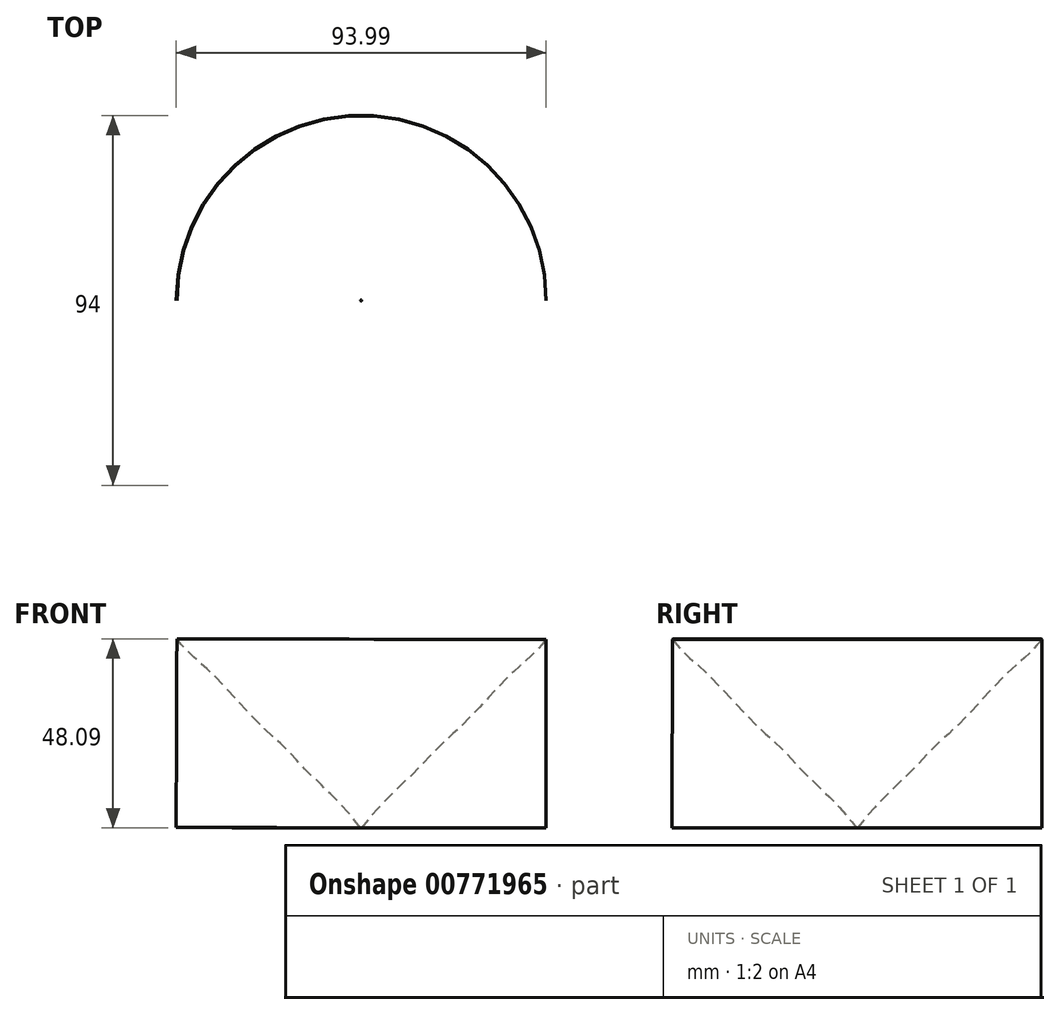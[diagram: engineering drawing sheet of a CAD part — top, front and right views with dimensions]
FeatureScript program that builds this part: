
annotation { "Feature Type Name" : "Feature", "Feature Type Description" : "" }
export const myFeature = defineFeature(function(context is Context, id is Id, definition is map)
    precondition{}
    {
        {
            var Q0;
            Q0=qCreatedBy(makeId("Front.planeOp"),FACE);
            var sketch = newSketch(context, id + "F0", { "sketchPlane" : qUnion([Q0])});
            skPoint(sketch, "E0", {"position": v(0, 1.93) * mm});
            skPoint(sketch, "E1", {"position": v(1.69, 2.62) * mm});
            skPoint(sketch, "E2", {"position": v(3.49, 4.29) * mm});
            skPoint(sketch, "E3", {"position": v(5.84, 6.5) * mm});
            skPoint(sketch, "E4", {"position": v(7.23, 8.44) * mm});
            skPoint(sketch, "E5", {"position": v(9.45, 10.38) * mm});
            skPoint(sketch, "E6", {"position": v(12.08, 12.73) * mm});
            skPoint(sketch, "E7", {"position": v(13.32, 14.26) * mm});
            skPoint(sketch, "E8", {"position": v(14.7, 15.5) * mm});
            skPoint(sketch, "E9", {"position": v(15.95, 16.61) * mm});
            skPoint(sketch, "E10", {"position": v(17.06, 17.72) * mm});
            skPoint(sketch, "E11", {"position": v(18.3, 19.38) * mm});
            skPoint(sketch, "E12", {"position": v(19.7, 20.77) * mm});
            skPoint(sketch, "E13", {"position": v(20.94, 21.74) * mm});
            skPoint(sketch, "E14", {"position": v(22.33, 23.12) * mm});
            skPoint(sketch, "E15", {"position": v(24.27, 24.92) * mm});
            skPoint(sketch, "E16", {"position": v(25.51, 26.59) * mm});
            skPoint(sketch, "E17", {"position": v(26.9, 27.7) * mm});
            skPoint(sketch, "E18", {"position": v(28.7, 29.77) * mm});
            skPoint(sketch, "E19", {"position": v(30.64, 31.43) * mm});
            skPoint(sketch, "E20", {"position": v(32.3, 33.23) * mm});
            skPoint(sketch, "E21", {"position": v(33.4, 34.48) * mm});
            skPoint(sketch, "E22", {"position": v(34.51, 35.87) * mm});
            skPoint(sketch, "E23", {"position": v(36.45, 38.08) * mm});
            skPoint(sketch, "E24", {"position": v(38.53, 39.74) * mm});
            skPoint(sketch, "E25", {"position": v(40.6, 41.4) * mm});
            skPoint(sketch, "E26", {"position": v(41.72, 42.51) * mm});
            skPoint(sketch, "E27", {"position": v(43.38, 43.9) * mm});
            skPoint(sketch, "E28", {"position": v(45.04, 45.7) * mm});
            skPoint(sketch, "E29", {"position": v(46.86, 46.8) * mm});
            skFitSpline(sketch, "E30", {"points": [v(0, 0) * mm, v(3.49, 4.29) * mm, v(9.45, 10.38) * mm, v(14.7, 15.5) * mm, v(19.7, 20.77) * mm, v(24.27, 24.92) * mm, v(30.64, 31.43) * mm, v(38.53, 39.74) * mm, v(41.72, 42.51) * mm, v(45.04, 45.7) * mm, v(46.86, 47.91) * mm], "startDerivative": vector(34.23, 44.37) * mm, "endDerivative": vector(24.25, 31.62) * mm});
            skLineSegment(sketch, "E31", {"start": v(46.86, 47.91) * mm, "end": v(46.86, 0) * mm});
            skLineSegment(sketch, "E32", {"start": v(46.86, 0) * mm, "end": v(0, 0) * mm, "construction": true});
            skLineSegment(sketch, "E33", {"start": v(46.86, 0) * mm, "end": v(0, 0) * mm});
            skLineSegment(sketch, "E34", {"start": v(0, 0) * mm, "end": v(0, 50.25) * mm});
            skLineSegment(sketch, "E35", {"start": v(0, 1.93) * mm, "end": v(0.17, 1.93) * mm});
            skLineSegment(sketch, "E36", {"start": v(0, 0) * mm, "end": v(0, 59.37) * mm});
            skLineSegment(sketch, "E37", {"start": v(-0.13, 0) * mm, "end": v(0, 68.57) * mm});
            skSolve(sketch);
        }
        {
            var Q0;
            Q0=makeQuery(id+"F0.imprint","IMPRINT",FACE,{"disambiguationData":[TD([[makeQuery(id+"F0.imprint","IMPRINT",EDGE,{"derivedFrom":sQuery(id+"F0.wireOp",EDGE,"E30")}),-1.0]])]});
            var Q1;
            Q1=sQuery(id+"F0.wireOp",EDGE,"E37");
            revolve(context, id + "F1", {"surfaceOperationType" : NewSurfaceOperationType.NEW, "entities" : qUnion([Q0]), "axis" : qUnion([Q1]), "revolveType" : RevolveType.FULL});
        }
    });
